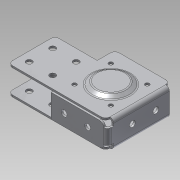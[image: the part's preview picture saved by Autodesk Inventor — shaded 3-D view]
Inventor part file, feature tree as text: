
AUTODESK INVENTOR PART (.ipt)
format: ipt  version: 2013 SP2 (Build 170200200, 200)  size: 319,488 bytes
history: native  units: mm
features: sketch x9, hole x4, sheet_metal_op x3, plane x3, fillet x2, extrude x2, loft x1, mirror x1, other x1
ambient origin geometry x8: Origin, YZ Plane, XZ Plane, XY Plane, X Axis, Y Axis, Z Axis, Center Point
bodies: Solid1 (feature_tree)
feature tree (26):
  sheet_metal_op  "Face1"
  hole  "Hole1"  [1 undecoded]
  hole  "Hole2"  [1 undecoded]
  sketch  "Sketch5"  dims[d7=39.9mm d8=9.95mm]
  plane  "Work Plane1"
  loft  "Loft1"
  fillet  "Fillet1"  Radius=1.6mm
  extrude  "Extrusion1"  Depth=9.95mm
  fillet  "Fillet2"  Radius=20.594885mm
  plane  "Work Plane2"
  mirror  "Mirror1"
  sheet_metal_op  "Bend1"
  hole  "Hole4"  [1 undecoded]
  extrude  "Extrusion2"  Depth=8.0mm
  hole  "Hole5"  [1 undecoded]
  sheet_metal_op  "Bend2"
  sketch  "Sketch1"  dims[d0=83.0mm d1=47.0mm]
  other  "Plate1"
  sketch  "Sketch2"  dims[d2=54.9mm d3=39.9mm]
  sketch  "Sketch3"  dims[d4=36.0mm d5=3.7mm d6=1.6mm]
  sketch  "Sketch6"  dims[d9=20.0mm d11=20.0mm d12=20.0mm d14=20.0mm]
  sketch  "Sketch7"  dims[d17=5.0mm d18=6.0mm d19=4.0mm d20=2.0mm d21=90.0deg d22=1.6mm d23=20.594885mm]
  plane  "Work Plane3"
  sketch  "Sketch8"  dims[d26=36.0mm d27=8.0mm]
  sketch  "Sketch9"  dims[d28=47.0mm d29=8.0mm]
  sketch  "Sketch10"  dims[d30=20.0mm d32=31.0mm d33=20.0mm d35=31.0mm d38=3.6mm d39=6.0mm d40=4.0mm d41=2.0mm d42=90.0deg d43=1.6mm d44=20.594885mm d56=15.5mm d57=15.5mm d58=32.3mm d59=2.6mm d60=24.7mm d61=0.0mm d62=90.0deg d63=0.0mm d64=90.0deg d65=2.0mm d66=1.6mm d67=2.6mm d68=-8.726646mm d69=2.0mm d70=10.0mm d71=1.6mm d72=0.8mm d73=3.2mm d74=1.6mm d75=1.6mm d80=47.5mm d81=11.5mm d82=20.0mm d83=16.0mm d84=5.0mm d85=6.0mm d86=4.0mm d87=2.0mm d88=90.0deg d89=1.6mm d90=20.594885mm d91=20.0mm d93=44.7mm d94=3.7mm d95=1.6mm d96=0.0mm d97=20.0mm d99=11.0mm d100=5.0mm d101=6.0mm d102=4.0mm d103=2.0mm d104=90.0deg d105=1.6mm d106=20.594885mm d107=1.6mm d108=0.8mm d109=3.2mm d110=1.6mm d111=1.6mm]
note: 4 required parameter values undecoded (feature->parameter linkage not recoverable at this tier; creation-order binding heuristic only, values carry confidence <= 0.55)
